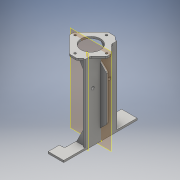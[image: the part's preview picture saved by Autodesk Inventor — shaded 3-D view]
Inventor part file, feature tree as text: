
AUTODESK INVENTOR PART (.ipt)
format: ipt  version: 2016 (Build 200138000, 138)  size: 287,744 bytes
history: native  units: mm
features: reference x14, sketch x12, extrude x10, fillet x3, plane x2, mirror x2, chamfer x1
ambient origin geometry x8: Origin, YZ Plane, XZ Plane, XY Plane, X Axis, Y Axis, Z Axis, Center Point
bodies: Solid1 (feature_tree)
feature tree (44):
  extrude  "Extrusion1"  Depth=13.0mm
  fillet  "Fillet1"  Radius=30.0mm
  extrude  "Extrusion2"  Depth=55.0mm
  extrude  "Extrusion3"  Depth=16.0mm
  extrude  "Extrusion4"  Depth=7.0mm
  extrude  "Extrusion5"  Depth=6.0mm
  chamfer  "Chamfer1"  Distance=241.0mm
  fillet  "Fillet2"  Radius=6.0mm
  extrude  "Extrusion6"  Depth=10.0mm
  extrude  "Extrusion7"  Depth=4.0mm
  plane  "Work Plane1"
  plane  "Work Plane2"
  sketch  "Sketch8"  dims[d20=4.0mm d23=7.0mm d24=0.0mm]
  extrude  "Extrusion8"  Depth=7.0mm TaperAngle=0.0deg
  mirror  "Mirror1"
  extrude  "Extrusion9"  Depth=6.0mm
  mirror  "Mirror2"
  sketch  "Sketch11"  dims[d33=0.5mm]
  extrude  "Extrusion10"  Depth=13.0mm TaperAngle=45.0deg
  fillet  "Fillet3"  Radius=7.0mm
  sketch  "Sketch1"  dims[d0=230.0mm d1=13.0mm d2=30.0mm]
  reference  "Reference1"
  sketch  "Sketch2"  dims[d3=55.0mm d4=55.0mm]
  reference  "Reference2"
  reference  "Reference3"
  sketch  "Sketch3"  dims[d5=55.0mm d6=16.0mm]
  sketch  "Sketch4"  dims[d7=6.0mm d8=0.0mm d9=7.0mm]
  reference  "Reference4"
  reference  "Reference5"
  reference  "Reference6"
  reference  "Reference7"
  sketch  "Sketch5"  dims[d10=100.0mm d11=6.0mm d12=241.0mm d13=0.0mm d14=6.0mm]
  sketch  "Sketch6"  dims[d15=85.0mm d16=0.0mm d17=10.0mm]
  reference  "Reference8"
  reference  "Reference9"
  reference  "Reference10"
  reference  "Reference11"
  reference  "Reference12"
  sketch  "Sketch7"  dims[d18=10.0mm d19=4.0mm]
  reference  "Reference13"
  reference  "Reference14"
  sketch  "Sketch9"  dims[d25=6.0mm d26=40.0mm]
  sketch  "Sketch10"  dims[d27=26.0mm d28=0.0mm d29=13.0mm d30=2.0mm d31=45.0deg d32=7.0mm]
  sketch  "Sketch12"  dims[d34=7.0mm d35=0.0mm d36=7.0mm d37=0.0mm d38=-10.0mm d39=25.0mm d40=50.0mm d41=6.0mm d42=0.0mm d43=30.0mm d45=50.0mm d46=6.0mm d47=0.0mm d48=90.0mm d49=90.0mm d50=90.0deg d51=45.0deg d52=20.0mm d53=6.0mm d54=0.0mm d55=7.0mm]
